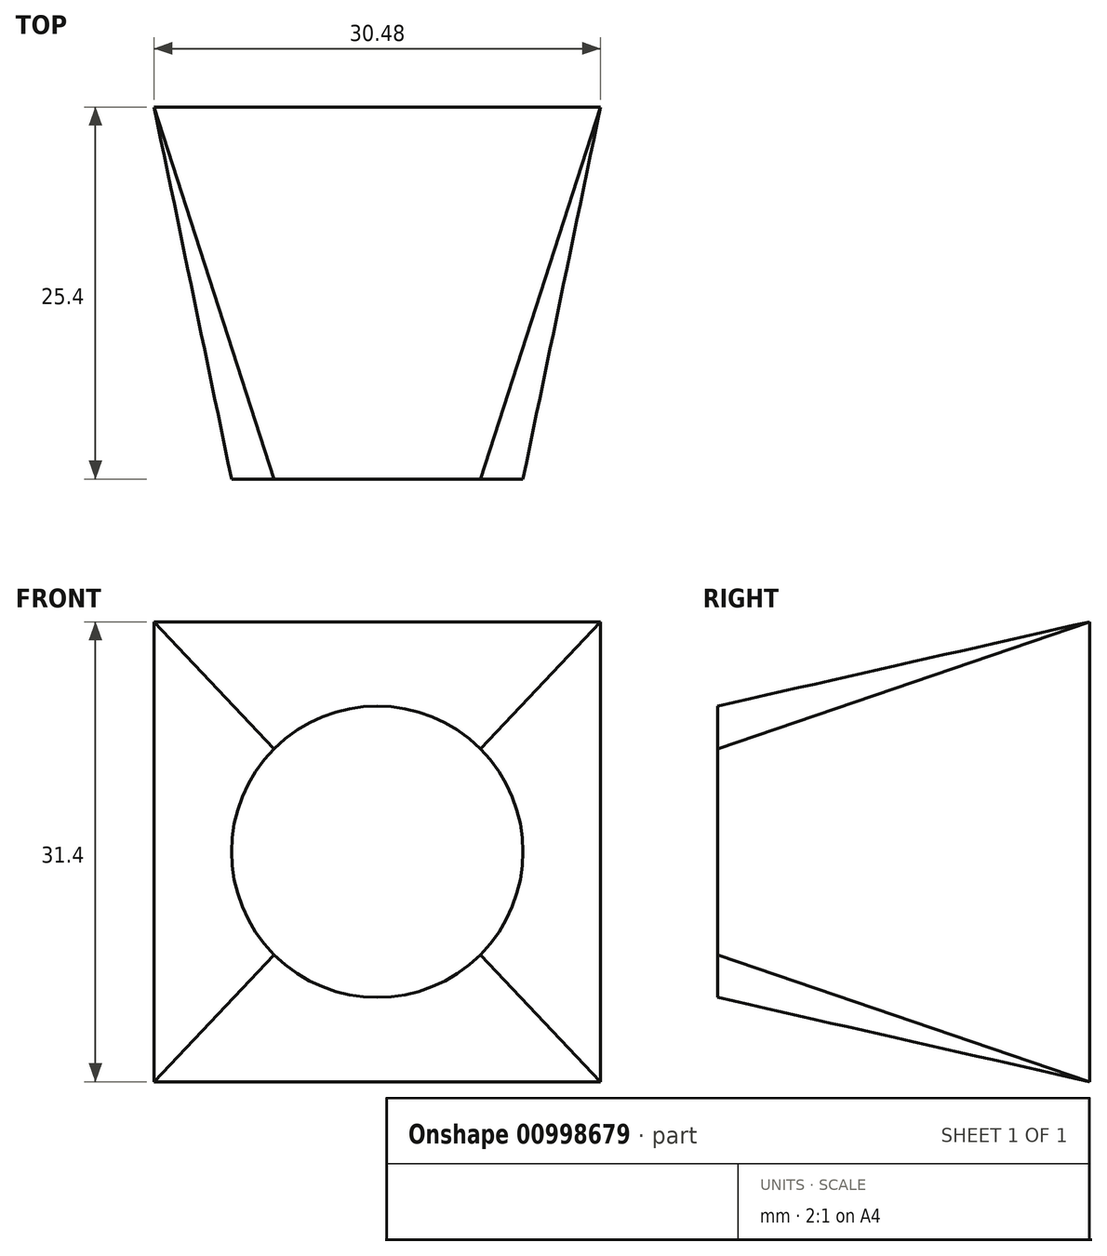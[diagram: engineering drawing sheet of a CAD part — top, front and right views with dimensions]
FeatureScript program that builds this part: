
annotation { "Feature Type Name" : "Feature", "Feature Type Description" : "" }
export const myFeature = defineFeature(function(context is Context, id is Id, definition is map)
    precondition{}
    {
        {
            var Q0;
            Q0=qCreatedBy(makeId("Front.planeOp"),FACE);
            cPlane(context, id + "F0", {"entities" : qUnion([Q0]), "cplaneType" : CPlaneType.OFFSET, "offset" : 25.4 * mm, "width" : 152.4 * mm, "height" : 152.4 * mm});
        }
        {
            var Q0;
            Q0=qCreatedBy(makeId("Front.planeOp"),FACE);
            var sketch = newSketch(context, id + "F1", { "sketchPlane" : qUnion([Q0])});
            skLineSegment(sketch, "E0.bottom", {"start": v(-15.24, 15.7) * mm, "end": v(15.24, 15.7) * mm});
            skLineSegment(sketch, "E0.top", {"start": v(-15.24, -15.7) * mm, "end": v(15.24, -15.7) * mm});
            skLineSegment(sketch, "E0.left", {"start": v(-15.24, 15.7) * mm, "end": v(-15.24, -15.7) * mm});
            skLineSegment(sketch, "E0.right", {"start": v(15.24, 15.7) * mm, "end": v(15.24, -15.7) * mm});
            skPoint(sketch, "E0.middle", {"position": v(0, 0) * mm});
            skSolve(sketch);
        }
        {
            var Q0;
            Q0=qCreatedBy(id+"F0.planeOp",FACE);
            var sketch = newSketch(context, id + "F2", { "sketchPlane" : qUnion([Q0])});
            skLineSegment(sketch, "E1", {"start": v(0, 0) * mm, "end": v(15, 15) * mm, "construction": true});
            skLineSegment(sketch, "E2", {"start": v(0, 0) * mm, "end": v(15.24, -15.24) * mm, "construction": true});
            skLineSegment(sketch, "E3", {"start": v(0, 0) * mm, "end": v(-7.03, -7.03) * mm, "construction": true});
            skLineSegment(sketch, "E4", {"start": v(0, 0) * mm, "end": v(-15.12, 15.12) * mm, "construction": true});
            skArc(sketch, "E5", {"start": v(7.03, 7.03) * mm, "mid": v(0, 9.95) * mm, "end": v(-7.03, 7.03) * mm});
            skArc(sketch, "E6", {"start": v(7.03, -7.03) * mm, "mid": v(9.95, 0) * mm, "end": v(7.03, 7.03) * mm});
            skLineSegment(sketch, "E7", {"start": v(-7.03, -7.03) * mm, "end": v(-15.12, -15.12) * mm, "construction": true});
            skArc(sketch, "E8", {"start": v(-7.03, 7.03) * mm, "mid": v(-7.03, -7.03) * mm, "end": v(7.03, -7.03) * mm});
            skSolve(sketch);
        }
        {
            var Q0;
            Q0=makeQuery(id+"F1.imprint","IMPRINT",FACE,{"disambiguationData":[TD([[makeQuery(id+"F1.imprint","IMPRINT",EDGE,{"derivedFrom":sQuery(id+"F1.wireOp",EDGE,"E0.bottom")}),-1.0]])]});
            var Q1;
            Q1=makeQuery(id+"F2.imprint","IMPRINT",FACE,{"disambiguationData":[TD([[makeQuery(id+"F2.imprint","IMPRINT",EDGE,{"derivedFrom":sQuery(id+"F2.wireOp",EDGE,"E5")}),1.0]])]});
            loft(context, id + "F3", {"sheetProfilesArray" : [{ "sheetProfileEntities" : qUnion([Q0]) }, { "sheetProfileEntities" : qUnion([Q1]) }]});
        }
    });
